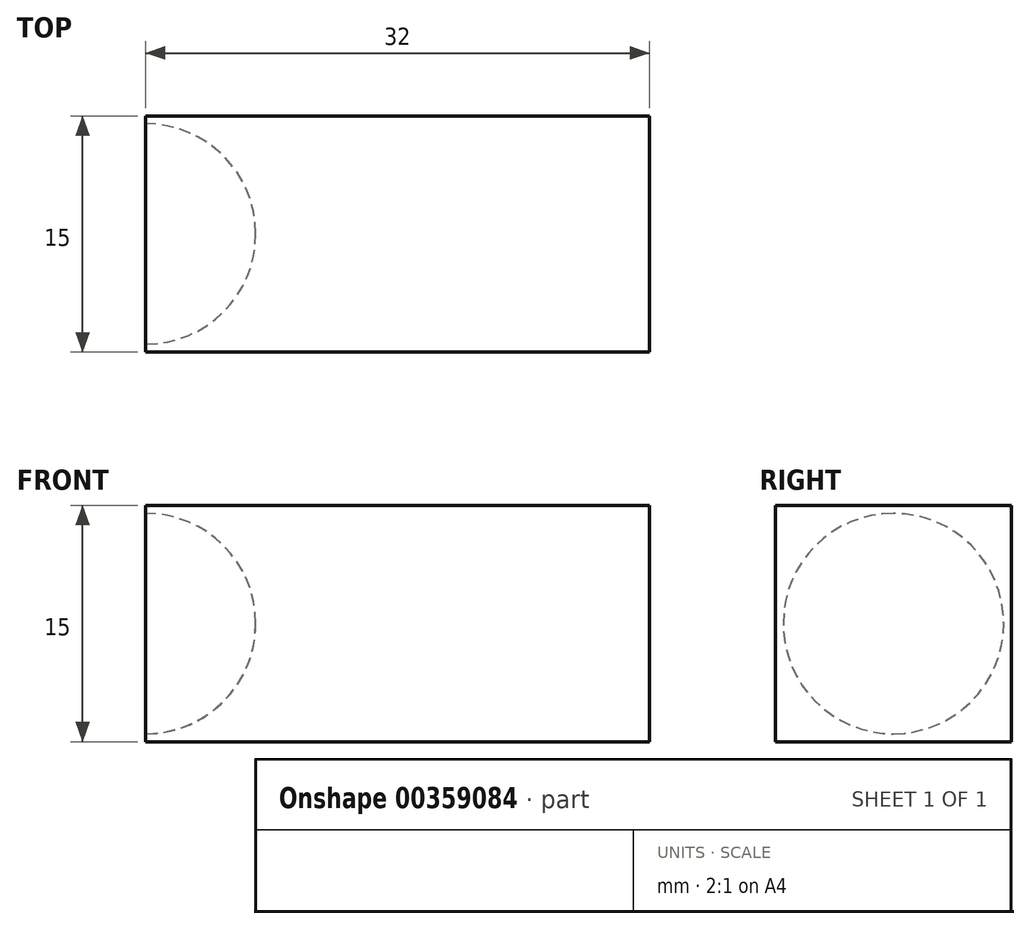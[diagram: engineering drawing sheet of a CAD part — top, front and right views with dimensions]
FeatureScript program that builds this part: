
annotation { "Feature Type Name" : "Feature", "Feature Type Description" : "" }
export const myFeature = defineFeature(function(context is Context, id is Id, definition is map)
    precondition{}
    {
        {
            var Q0;
            Q0=qCreatedBy(makeId("Top.planeOp"),FACE);
            var sketch = newSketch(context, id + "F0", { "sketchPlane" : qUnion([Q0])});
            skLineSegment(sketch, "E0.bottom", {"start": v(0, 0) * mm, "end": v(40, 0) * mm});
            skLineSegment(sketch, "E0.top", {"start": v(0, 15) * mm, "end": v(40, 15) * mm});
            skLineSegment(sketch, "E0.left", {"start": v(0, 0) * mm, "end": v(0, 15) * mm});
            skLineSegment(sketch, "E0.right", {"start": v(40, 0) * mm, "end": v(40, 15) * mm});
            skSolve(sketch);
        }
        {
            var Q0;
            Q0 = qSketchRegion(id + "F0", true);
            extrude(context, id + "F1", {"entities" : qUnion([Q0]), "depth" : 15 * mm});
        }
        {
            var Q0;
            Q0=makeQuery(id+"F1.opExtrude","SWEPT_FACE",FACE,{"disambiguationData":[OSD([sQuery(id+"F0.wireOp",EDGE,"E0.left")])]});
            var sketch = newSketch(context, id + "F2", { "sketchPlane" : qUnion([Q0])});
            skLineSegment(sketch, "E1.bottom", {"start": v(-15, 15) * mm, "end": v(0, 15) * mm});
            skLineSegment(sketch, "E1.top", {"start": v(-15, 0) * mm, "end": v(0, 0) * mm});
            skLineSegment(sketch, "E1.left", {"start": v(-15, 15) * mm, "end": v(-15, 0) * mm});
            skLineSegment(sketch, "E1.right", {"start": v(0, 15) * mm, "end": v(0, 0) * mm});
            skLineSegment(sketch, "E2.bottom", {"start": v(-14.5, 14.5) * mm, "end": v(-0.5, 14.5) * mm});
            skLineSegment(sketch, "E2.top", {"start": v(-14.5, 0.5) * mm, "end": v(-0.5, 0.5) * mm});
            skLineSegment(sketch, "E2.left", {"start": v(-14.5, 14.5) * mm, "end": v(-14.5, 0.5) * mm});
            skLineSegment(sketch, "E2.right", {"start": v(-0.5, 14.5) * mm, "end": v(-0.5, 0.5) * mm});
            skSolve(sketch);
        }
        {
            var Q0;
            Q0=makeQuery(id+"F2.imprint","IMPRINT",FACE,{"disambiguationData":[TD([[makeQuery(id+"F2.imprint","IMPRINT",EDGE,{"derivedFrom":sQuery(id+"F2.wireOp",EDGE,"E2.bottom")}),-1.0]])]});
            extrude(context, id + "F3", {"entities" : qUnion([Q0]), "operationType" : NewBodyOperationType.REMOVE, "oppositeDirection" : true, "depth" : 15 * mm});
        }
        {
            var Q0;
            Q0=makeQuery(id+"F3.boolean.opBoolean","COPY",EDGE,{"derivedFrom":makeQuery(id+"F3.opExtrude","CAP_EDGE",EDGE,{"disambiguationData":[OSD([sQuery(id+"F2.wireOp",EDGE,"E2.bottom")])],"isStart":false})});
            var Q1;
            Q1=makeQuery(id+"F3.boolean.opBoolean","COPY",EDGE,{"derivedFrom":makeQuery(id+"F3.opExtrude","CAP_EDGE",EDGE,{"disambiguationData":[OSD([sQuery(id+"F2.wireOp",EDGE,"E2.left")])],"isStart":false})});
            var Q2;
            Q2=makeQuery(id+"F3.boolean.opBoolean","COPY",EDGE,{"derivedFrom":makeQuery(id+"F3.opExtrude","SWEPT_EDGE",EDGE,{"disambiguationData":[OSD([sQuery(id+"F2.wireOp",EDGE,"E2.bottom"),sQuery(id+"F2.wireOp",EDGE,"E2.left")])]})});
            var Q3;
            Q3=makeQuery(id+"F3.boolean.opBoolean","COPY",EDGE,{"derivedFrom":makeQuery(id+"F3.opExtrude","CAP_EDGE",EDGE,{"disambiguationData":[OSD([sQuery(id+"F2.wireOp",EDGE,"E2.right")])],"isStart":false})});
            var Q4;
            Q4=makeQuery(id+"F3.boolean.opBoolean","COPY",EDGE,{"derivedFrom":makeQuery(id+"F3.opExtrude","CAP_EDGE",EDGE,{"disambiguationData":[OSD([sQuery(id+"F2.wireOp",EDGE,"E2.top")])],"isStart":false})});
            var Q5;
            Q5=makeQuery(id+"F3.boolean.opBoolean","COPY",EDGE,{"derivedFrom":makeQuery(id+"F3.opExtrude","SWEPT_EDGE",EDGE,{"disambiguationData":[OSD([sQuery(id+"F2.wireOp",EDGE,"E2.bottom"),sQuery(id+"F2.wireOp",EDGE,"E2.right")])]})});
            var Q6;
            Q6=makeQuery(id+"F3.boolean.opBoolean","COPY",EDGE,{"derivedFrom":makeQuery(id+"F3.opExtrude","SWEPT_EDGE",EDGE,{"disambiguationData":[OSD([sQuery(id+"F2.wireOp",EDGE,"E2.top"),sQuery(id+"F2.wireOp",EDGE,"E2.right")])]})});
            var Q7;
            Q7=makeQuery(id+"F3.boolean.opBoolean","COPY",EDGE,{"derivedFrom":makeQuery(id+"F3.opExtrude","SWEPT_EDGE",EDGE,{"disambiguationData":[OSD([sQuery(id+"F2.wireOp",EDGE,"E2.top"),sQuery(id+"F2.wireOp",EDGE,"E2.left")])]})});
            fillet(context, id + "F4", {"entities" : qUnion([Q0, Q1, Q2, Q3, Q4, Q5, Q6, Q7]), "radius" : 7 * mm, "tangentPropagation" : true, "allowEdgeOverflow" : false});
        }
        {
            var Q0;
            Q0=makeQuery(id+"F1.opExtrude","SWEPT_FACE",FACE,{"disambiguationData":[OSD([sQuery(id+"F0.wireOp",EDGE,"E0.left")])]});
            extrude(context, id + "F5", {"entities" : qUnion([Q0]), "operationType" : NewBodyOperationType.REMOVE, "oppositeDirection" : true, "depth" : 8 * mm});
        }
    });
